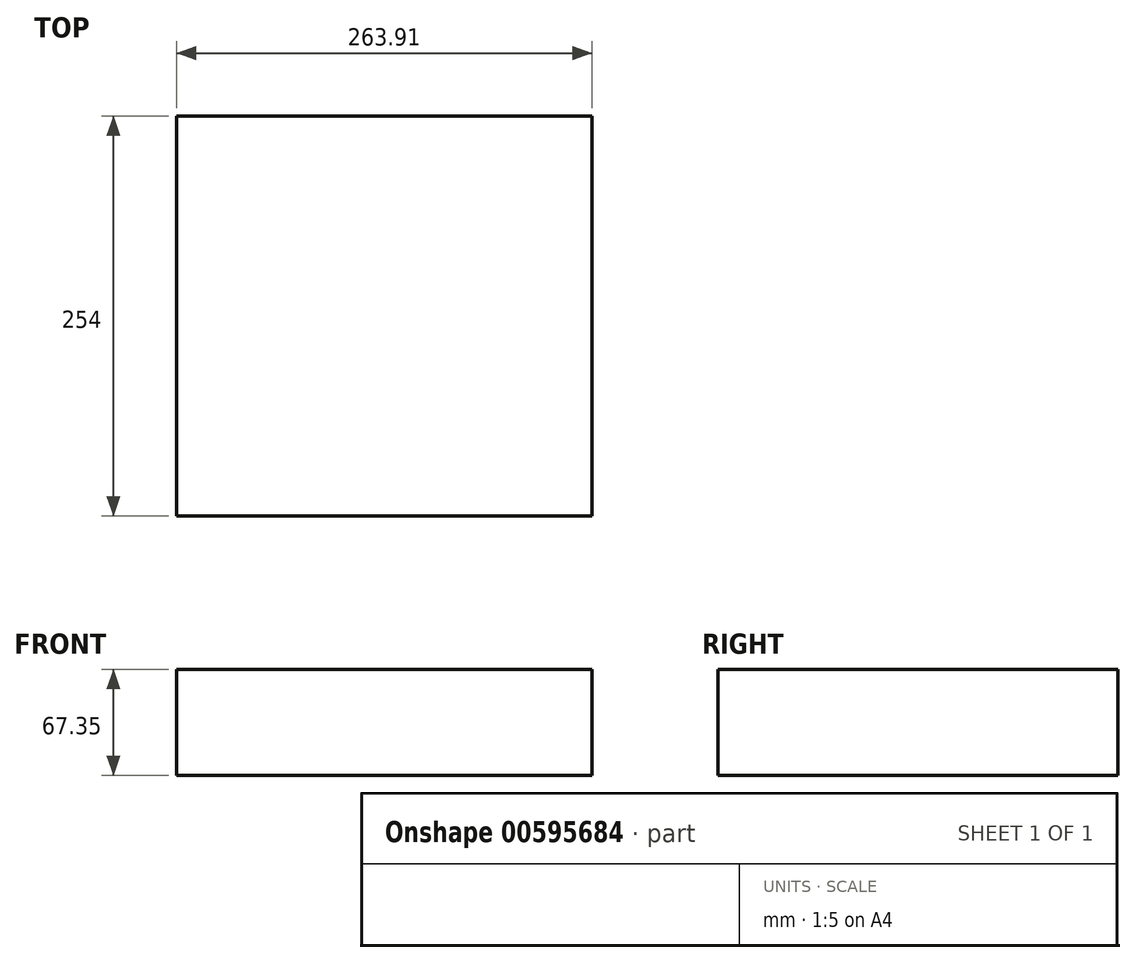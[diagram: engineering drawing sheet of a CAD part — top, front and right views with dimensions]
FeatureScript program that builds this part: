
annotation { "Feature Type Name" : "Feature", "Feature Type Description" : "" }
export const myFeature = defineFeature(function(context is Context, id is Id, definition is map)
    precondition{}
    {
        {
            var Q0;
            Q0=qCreatedBy(makeId("Front.planeOp"),FACE);
            var sketch = newSketch(context, id + "F0", { "sketchPlane" : qUnion([Q0])});
            skLineSegment(sketch, "E0.bottom", {"start": v(-125.54, -67.35) * mm, "end": v(138.37, -67.35) * mm});
            skLineSegment(sketch, "E0.top", {"start": v(-125.54, 0) * mm, "end": v(138.37, 0) * mm});
            skLineSegment(sketch, "E0.left", {"start": v(-125.54, -67.35) * mm, "end": v(-125.54, 0) * mm});
            skLineSegment(sketch, "E0.right", {"start": v(138.37, -67.35) * mm, "end": v(138.37, 0) * mm});
            skSolve(sketch);
        }
        {
            var Q0;
            Q0=makeQuery(id+"F0.imprint","IMPRINT",FACE,{"disambiguationData":[TD([[makeQuery(id+"F0.imprint","IMPRINT",EDGE,{"derivedFrom":sQuery(id+"F0.wireOp",EDGE,"E0.bottom")}),1.0]])]});
            extrude(context, id + "F1", {"entities" : qUnion([Q0]), "endBound" : BoundingType.SYMMETRIC, "depth" : 254 * mm, "offsetDistance" : 25.4 * mm});
        }
    });
